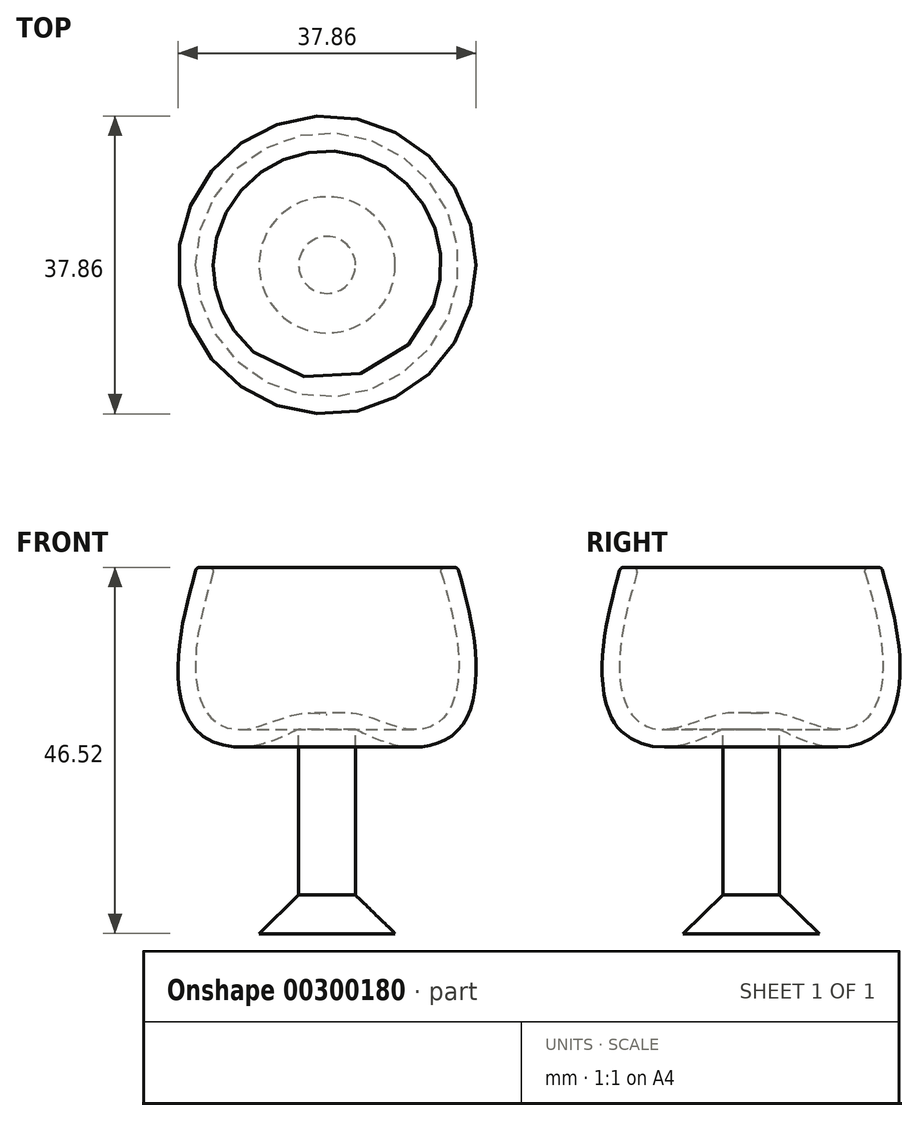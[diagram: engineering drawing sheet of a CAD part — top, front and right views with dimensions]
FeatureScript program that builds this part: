
annotation { "Feature Type Name" : "Feature", "Feature Type Description" : "" }
export const myFeature = defineFeature(function(context is Context, id is Id, definition is map)
    precondition{}
    {
        {
            var Q0;
            Q0=qCreatedBy(makeId("Front.planeOp"),FACE);
            var sketch = newSketch(context, id + "F0", { "sketchPlane" : qUnion([Q0])});
            skLineSegment(sketch, "E0", {"start": v(-3.6, -21.05) * mm, "end": v(-3.6, 0) * mm});
            skFitSpline(sketch, "E1", {"points": [v(-3.6, 0) * mm, v(-10.4, -2.24) * mm, v(-16.74, 0) * mm, v(-18.9, 8.73) * mm, v(-16.6, 20.57) * mm], "startDerivative": vector(-28.98, -13.7) * mm, "endDerivative": vector(10.85, 40.12) * mm});
            skLineSegment(sketch, "E2", {"start": v(-16.6, 20.57) * mm, "end": v(-14.3, 20.57) * mm});
            skLineSegment(sketch, "E3", {"start": v(0, 1.9) * mm, "end": v(0, -25.95) * mm});
            skFitSpline(sketch, "E4", {"points": [v(-14.3, 20.57) * mm, v(-16.74, 8.6) * mm, v(-14.9, 1.6) * mm, v(-10.5, 0) * mm, v(-3.96, 1.9) * mm, v(0, 1.9) * mm], "startDerivative": vector(-13.01, -45.9) * mm, "endDerivative": vector(23.98, -3.16) * mm});
            skLineSegment(sketch, "E5", {"start": v(0, 1.9) * mm, "end": v(0, -25.95) * mm, "construction": true});
            skPoint(sketch, "E6.orphan", {"position": v(0, 20.57) * mm});
            skLineSegment(sketch, "E7", {"start": v(0, -25.95) * mm, "end": v(-8.65, -25.95) * mm});
            skLineSegment(sketch, "E8", {"start": v(-8.65, -25.95) * mm, "end": v(-3.6, -21.05) * mm});
            skSolve(sketch);
        }
        {
            var Q0;
            Q0 = qSketchRegion(id + "F0", true);
            var Q1;
            Q1=sQuery(id+"F0.wireOp",EDGE,"E3");
            revolve(context, id + "F1", {"entities" : qUnion([Q0]), "axis" : qUnion([Q1]), "revolveType" : RevolveType.FULL});
        }
        {
            var Q0;
            Q0=makeQuery(id+"F1.opRevolve","SWEPT_EDGE",EDGE,{"disambiguationData":[OSD([sQuery(id+"F0.wireOp",EDGE,"E1"),sQuery(id+"F0.wireOp",EDGE,"E2")])]});
            var Q1;
            Q1=makeQuery(id+"F1.opRevolve","SWEPT_EDGE",EDGE,{"disambiguationData":[OSD([sQuery(id+"F0.wireOp",EDGE,"E2"),sQuery(id+"F0.wireOp",EDGE,"E4")])]});
            fillet(context, id + "F2", {"entities" : qUnion([Q0, Q1]), "radius" : 0.5 * mm, "tangentPropagation" : true, "allowEdgeOverflow" : false});
        }
    });
